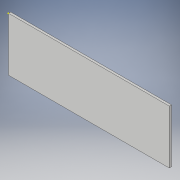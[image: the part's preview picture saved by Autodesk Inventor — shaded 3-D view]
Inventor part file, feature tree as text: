
AUTODESK INVENTOR PART (.ipt)
format: ipt  version: 2017 (Build 210142000, 142)  size: 88,064 bytes
history: native  units: in
note: dims shown in document units (in); Inventor stores cm internally (conversion verified against a paired STEP export)
features: sketch x2, extrude x1
ambient origin geometry x8: Origin, YZ Plane, XZ Plane, XY Plane, X Axis, Y Axis, Z Axis, Center Point
bodies: Solid1 (feature_tree)
feature tree (3):
  extrude  "Extrusion1"  Depth=24.0in
  sketch  "Sketch2"  dims[d2=1.0in d3=0.0in]
  sketch  "Sketch1"  dims[d0=72.0in d1=24.0in]
